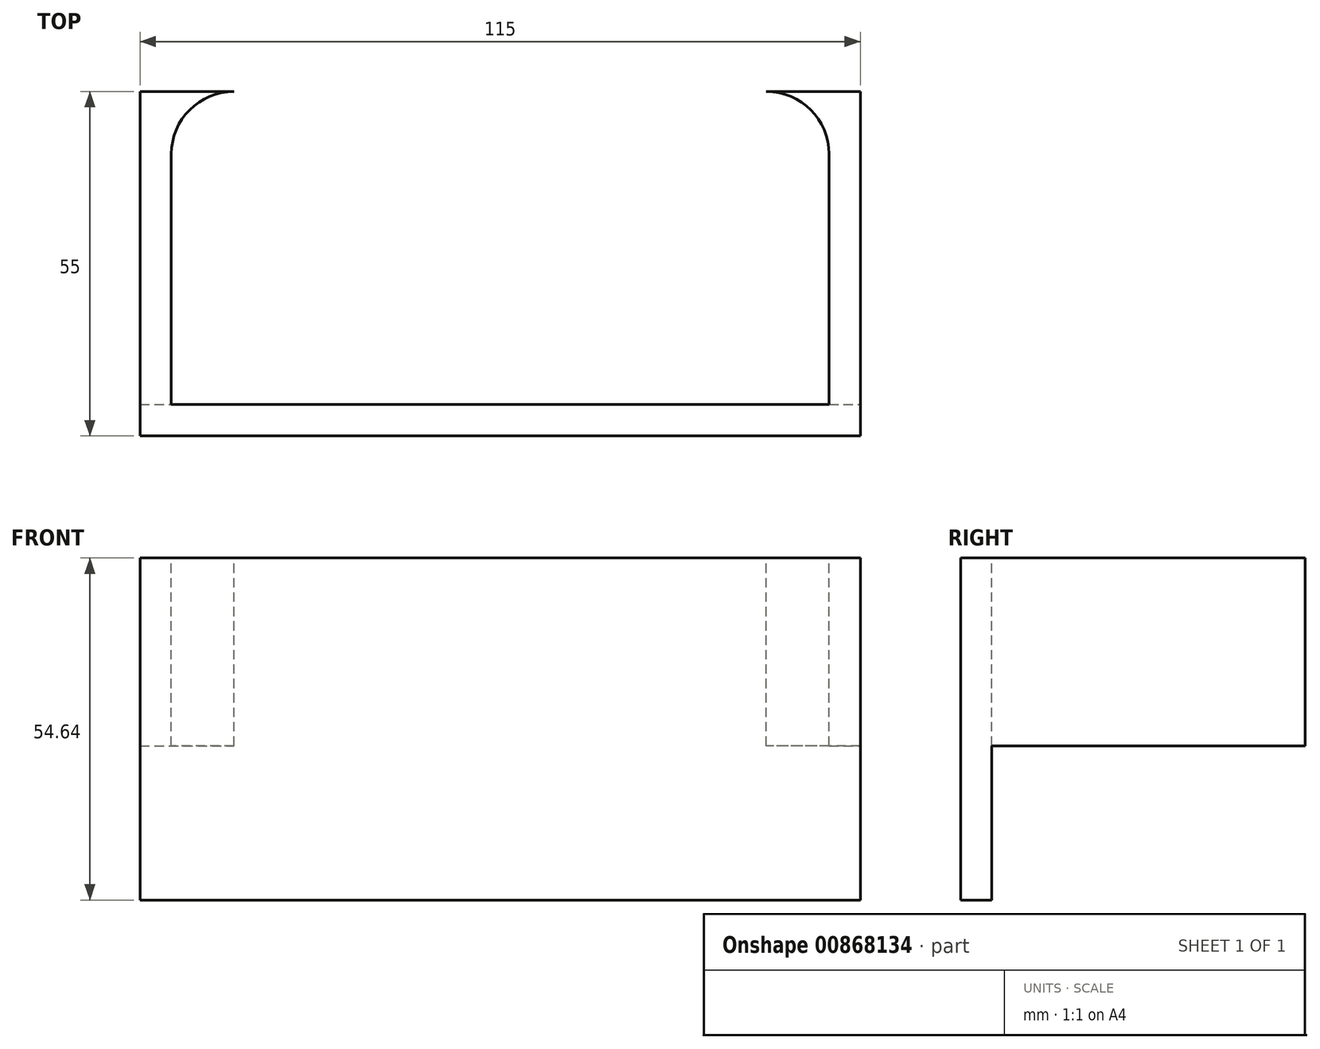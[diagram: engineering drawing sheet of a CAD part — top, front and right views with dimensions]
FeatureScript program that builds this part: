
annotation { "Feature Type Name" : "Feature", "Feature Type Description" : "" }
export const myFeature = defineFeature(function(context is Context, id is Id, definition is map)
    precondition{}
    {
        {
            var Q0;
            Q0=qCreatedBy(makeId("Front.planeOp"),FACE);
            var sketch = newSketch(context, id + "F0", { "sketchPlane" : qUnion([Q0])});
            skLineSegment(sketch, "E0.bottom", {"start": v(-57.5, 27) * mm, "end": v(57.5, 27) * mm});
            skLineSegment(sketch, "E0.top", {"start": v(-57.5, -27.64) * mm, "end": v(57.5, -27.64) * mm});
            skLineSegment(sketch, "E0.left", {"start": v(-57.5, 27) * mm, "end": v(-57.5, -27.64) * mm});
            skLineSegment(sketch, "E0.right", {"start": v(57.5, 27) * mm, "end": v(57.5, -27.64) * mm});
            skLineSegment(sketch, "E1", {"start": v(0, 0) * mm, "end": v(0, 57.68) * mm, "construction": true});
            skSolve(sketch);
        }
        {
            var Q0;
            Q0=makeQuery(id+"F0.imprint","IMPRINT",FACE,{"disambiguationData":[TD([[makeQuery(id+"F0.imprint","IMPRINT",EDGE,{"derivedFrom":sQuery(id+"F0.wireOp",EDGE,"E0.bottom")}),-1.0]])]});
            extrude(context, id + "F1", {"entities" : qUnion([Q0]), "oppositeDirection" : true, "depth" : 5 * mm, "offsetDistance" : 25 * mm});
        }
        {
            var Q0;
            Q0=makeQuery(id+"F1.opExtrude","SWEPT_FACE",FACE,{"disambiguationData":[OSD([sQuery(id+"F0.wireOp",EDGE,"E0.bottom")])]});
            var sketch = newSketch(context, id + "F2", { "sketchPlane" : qUnion([Q0])});
            skLineSegment(sketch, "E2.bottom", {"start": v(-57.5, 5) * mm, "end": v(-52.5, 5) * mm});
            skLineSegment(sketch, "E2.top", {"start": v(-57.5, 55) * mm, "end": v(-42.5, 55) * mm});
            skLineSegment(sketch, "E2.left", {"start": v(-57.5, 5) * mm, "end": v(-57.5, 55) * mm});
            skLineSegment(sketch, "E3", {"start": v(0, 0) * mm, "end": v(0, 92.29) * mm, "construction": true});
            skLineSegment(sketch, "E4", {"start": v(-52.5, 45) * mm, "end": v(-52.5, 5) * mm});
            skArc(sketch, "E5", {"start": v(-42.5, 55) * mm, "mid": v(-49.57, 52.07) * mm, "end": v(-52.5, 45) * mm});
            skLineSegment(sketch, "E6.MirrorCS", {"start": v(57.5, 5) * mm, "end": v(57.5, 55) * mm});
            skArc(sketch, "E7.MirrorCS", {"start": v(42.5, 55) * mm, "mid": v(49.57, 52.07) * mm, "end": v(52.5, 45) * mm});
            skLineSegment(sketch, "E8.MirrorCS", {"start": v(57.5, 5) * mm, "end": v(52.5, 5) * mm});
            skLineSegment(sketch, "E9.MirrorCS", {"start": v(57.5, 55) * mm, "end": v(42.5, 55) * mm});
            skLineSegment(sketch, "E10.MirrorCS", {"start": v(52.5, 45) * mm, "end": v(52.5, 5) * mm});
            skSolve(sketch);
        }
        {
            var Q0;
            Q0 = qSketchRegion(id + "F2", true);
            extrude(context, id + "F3", {"entities" : qUnion([Q0]), "operationType" : NewBodyOperationType.ADD, "oppositeDirection" : true, "depth" : 30 * mm, "offsetDistance" : 25 * mm});
        }
    });
